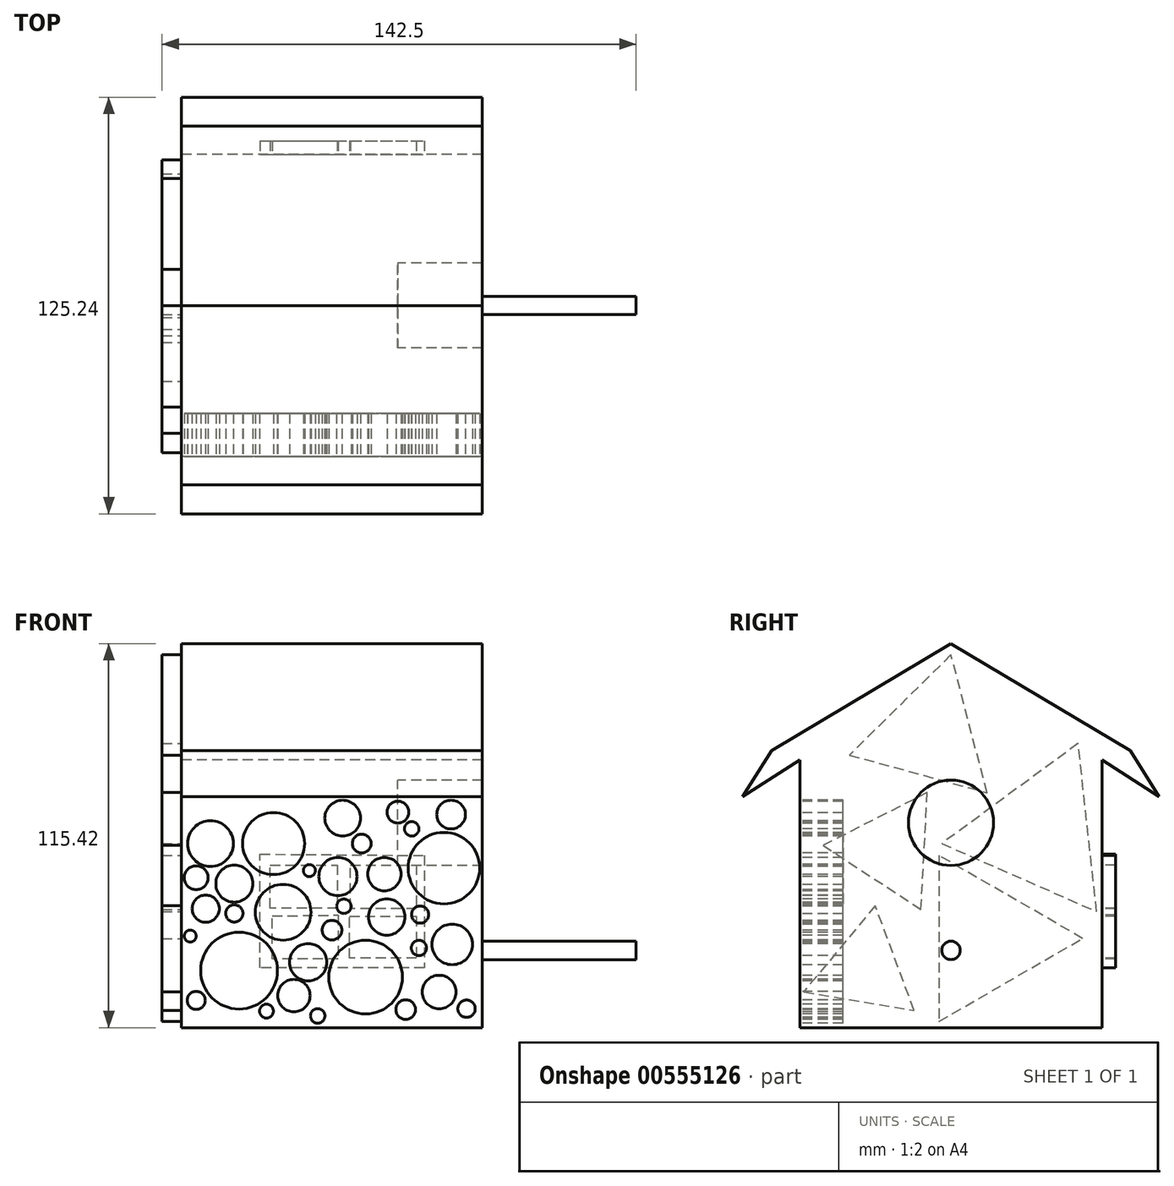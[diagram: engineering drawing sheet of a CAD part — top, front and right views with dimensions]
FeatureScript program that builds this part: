
annotation { "Feature Type Name" : "Feature", "Feature Type Description" : "" }
export const myFeature = defineFeature(function(context is Context, id is Id, definition is map)
    precondition{}
    {
        {
            var Q0;
            Q0=qCreatedBy(makeId("Right.planeOp"),FACE);
            var sketch = newSketch(context, id + "F0", { "sketchPlane" : qUnion([Q0])});
            skLineSegment(sketch, "E0", {"start": v(-45.42, 25.15) * mm, "end": v(0, 50.44) * mm});
            skLineSegment(sketch, "E1.MirrorCS", {"start": v(45.42, 25.15) * mm, "end": v(0, 50.44) * mm});
            skLineSegment(sketch, "E2", {"start": v(-45.42, 25.15) * mm, "end": v(-45.42, -55.32) * mm});
            skLineSegment(sketch, "E3", {"start": v(-45.42, -55.32) * mm, "end": v(45.42, -55.32) * mm});
            skLineSegment(sketch, "E4", {"start": v(45.42, -55.32) * mm, "end": v(45.42, 25.15) * mm});
            skCircle(sketch, "E5", {"center": v(0, 6.25) * mm, "radius": 12.8 * mm});
            skLineSegment(sketch, "E6", {"start": v(-45.42, 25.15) * mm, "end": v(-62.62, 14.07) * mm});
            skLineSegment(sketch, "E7", {"start": v(-62.62, 14.07) * mm, "end": v(-53.87, 27.88) * mm});
            skLineSegment(sketch, "E8", {"start": v(-53.87, 27.88) * mm, "end": v(0, 60.1) * mm});
            skLineSegment(sketch, "E9.MirrorCS", {"start": v(53.87, 27.88) * mm, "end": v(0, 60.1) * mm});
            skLineSegment(sketch, "E10.MirrorCS", {"start": v(62.62, 14.07) * mm, "end": v(53.87, 27.88) * mm});
            skLineSegment(sketch, "E11.MirrorCS", {"start": v(45.42, 25.15) * mm, "end": v(62.62, 14.07) * mm});
            skSolve(sketch);
        }
        {
            var Q0;
            Q0 = qSketchRegion(id + "F0", true);
            extrude(context, id + "F1", {"entities" : qUnion([Q0]), "depth" : 13.46 * mm, "offsetDistance" : 25.4 * mm});
        }
        {
            var Q0;
            Q0=qCreatedBy(makeId("Right.planeOp"),FACE);
            var sketch = newSketch(context, id + "F2", { "sketchPlane" : qUnion([Q0])});
            skCircle(sketch, "E12", {"center": v(0, -32.1) * mm, "radius": 2.78 * mm});
            skSolve(sketch);
        }
        {
            var Q0;
            Q0 = qSketchRegion(id + "F2", true);
            extrude(context, id + "F3", {"entities" : qUnion([Q0]), "operationType" : NewBodyOperationType.ADD, "depth" : 71.63 * mm, "offsetDistance" : 25.4 * mm});
        }
        {
            var Q0;
            Q0 = qSketchRegion(id + "F0", true);
            extrude(context, id + "F4", {"entities" : qUnion([Q0]), "operationType" : NewBodyOperationType.ADD, "depth" : 25.4 * mm, "offsetDistance" : 25.4 * mm});
        }
        {
            var Q0;
            Q0 = qSketchRegion(id + "F0", true);
            extrude(context, id + "F5", {"entities" : qUnion([Q0]), "operationType" : NewBodyOperationType.ADD, "depth" : 25.4 * mm, "offsetDistance" : 25.4 * mm});
        }
        {
            var Q0;
            Q0=makeQuery(id+"F1.opExtrude","CAP_FACE",FACE,{"disambiguationData":[OSD([sQuery(id+"F0.wireOp",EDGE,"E2"),sQuery(id+"F0.wireOp",EDGE,"E3"),sQuery(id+"F0.wireOp",EDGE,"E4"),sQuery(id+"F0.wireOp",EDGE,"E5"),sQuery(id+"F0.wireOp",EDGE,"E6"),sQuery(id+"F0.wireOp",EDGE,"E7"),sQuery(id+"F0.wireOp",EDGE,"E8"),sQuery(id+"F0.wireOp",EDGE,"E9.MirrorCS"),sQuery(id+"F0.wireOp",EDGE,"E10.MirrorCS"),sQuery(id+"F0.wireOp",EDGE,"E11.MirrorCS")])],"isStart":true});
            var sketch = newSketch(context, id + "F6", { "sketchPlane" : qUnion([Q0])});
            skLineSegment(sketch, "E13", {"start": v(0, 60.1) * mm, "end": v(-53.87, 27.88) * mm});
            skLineSegment(sketch, "E14", {"start": v(-53.87, 27.88) * mm, "end": v(-62.62, 14.07) * mm});
            skLineSegment(sketch, "E15", {"start": v(-62.62, 14.07) * mm, "end": v(-45.42, 25.15) * mm});
            skLineSegment(sketch, "E16", {"start": v(-45.42, 25.15) * mm, "end": v(-45.42, -55.32) * mm});
            skLineSegment(sketch, "E17", {"start": v(-45.42, -55.32) * mm, "end": v(45.42, -55.32) * mm});
            skLineSegment(sketch, "E18", {"start": v(45.42, -55.32) * mm, "end": v(45.42, 25.15) * mm});
            skLineSegment(sketch, "E19", {"start": v(45.42, 25.15) * mm, "end": v(62.62, 14.07) * mm});
            skLineSegment(sketch, "E20", {"start": v(62.62, 14.07) * mm, "end": v(53.87, 27.88) * mm});
            skLineSegment(sketch, "E21", {"start": v(53.87, 27.88) * mm, "end": v(0, 60.1) * mm});
            skSolve(sketch);
        }
        {
            var Q0;
            Q0 = qSketchRegion(id + "F6", true);
            extrude(context, id + "F7", {"entities" : qUnion([Q0]), "operationType" : NewBodyOperationType.ADD, "depth" : 65.02 * mm, "offsetDistance" : 25.4 * mm});
        }
        {
            var Q0;
            {var subQ0=sQuery(id+"F0.wireOp",EDGE,"E2");Q0=makeQuery(id+"F7.boolean.opBoolean","MERGE",FACE,{"derivedFrom":[makeQuery(id+"F4.boolean.opBoolean","MERGE",FACE,{"derivedFrom":[makeQuery(id+"F1.opExtrude","SWEPT_FACE",FACE,{"disambiguationData":[OSD([subQ0])]}),makeQuery(id+"F4.opExtrude","SWEPT_FACE",FACE,{"disambiguationData":[OSD([subQ0])]})]}),makeQuery(id+"F7.opExtrude","SWEPT_FACE",FACE,{"disambiguationData":[OSD([sQuery(id+"F6.wireOp",EDGE,"E18")])]})]});}
            var sketch = newSketch(context, id + "F8", { "sketchPlane" : qUnion([Q0])});
            skCircle(sketch, "E22", {"center": v(-47.74, -38.18) * mm, "radius": 11.54 * mm});
            skCircle(sketch, "E23", {"center": v(-49.17, -12.04) * mm, "radius": 5.56 * mm});
            skCircle(sketch, "E24", {"center": v(-34.49, -20.64) * mm, "radius": 8.38 * mm});
            skCircle(sketch, "E25", {"center": v(-37.35, 0) * mm, "radius": 9.32 * mm});
            skCircle(sketch, "E26", {"center": v(13.84, -7.4) * mm, "radius": 10.75 * mm});
            skCircle(sketch, "E27", {"center": v(-16.23, -18.85) * mm, "radius": 2.18 * mm});
            skCircle(sketch, "E28", {"center": v(-26.97, -35.67) * mm, "radius": 5.6 * mm});
            skCircle(sketch, "E29", {"center": v(-3.34, -22.07) * mm, "radius": 5.45 * mm});
            skCircle(sketch, "E30", {"center": v(6.68, -21.35) * mm, "radius": 2.58 * mm});
            skCircle(sketch, "E31", {"center": v(6.32, -31.38) * mm, "radius": 2.3 * mm});
            skCircle(sketch, "E32", {"center": v(16.35, -30.3) * mm, "radius": 6.1 * mm});
            skCircle(sketch, "E33", {"center": v(12.4, -44.62) * mm, "radius": 5.06 * mm});
            skCircle(sketch, "E34", {"center": v(20.64, -49.63) * mm, "radius": 2.6 * mm});
            skCircle(sketch, "E35", {"center": v(-4.06, -9.18) * mm, "radius": 5.02 * mm});
            skCircle(sketch, "E36", {"center": v(-26.61, -8.1) * mm, "radius": 1.83 * mm});
            skCircle(sketch, "E37", {"center": v(-18.02, -9.9) * mm, "radius": 5.74 * mm});
            skCircle(sketch, "E38", {"center": v(-16.6, 7.64) * mm, "radius": 5.38 * mm});
            skCircle(sketch, "E39", {"center": v(0, 9.43) * mm, "radius": 3.28 * mm});
            skCircle(sketch, "E40", {"center": v(15.99, 8.72) * mm, "radius": 4.31 * mm});
            skCircle(sketch, "E41", {"center": v(4.17, 4.42) * mm, "radius": 2.18 * mm});
            skCircle(sketch, "E42", {"center": v(-10.86, 0) * mm, "radius": 2.83 * mm});
            skCircle(sketch, "E43", {"center": v(-56.33, 0) * mm, "radius": 6.87 * mm});
            skCircle(sketch, "E44", {"center": v(-60.62, -10.25) * mm, "radius": 3.58 * mm});
            skCircle(sketch, "E45", {"center": v(-49.17, -21) * mm, "radius": 2.58 * mm});
            skCircle(sketch, "E46", {"center": v(-57.76, -19.56) * mm, "radius": 4.08 * mm});
            skCircle(sketch, "E47", {"center": v(-31.27, -45.7) * mm, "radius": 4.87 * mm});
            skCircle(sketch, "E48", {"center": v(-19.81, -26) * mm, "radius": 2.95 * mm});
            skCircle(sketch, "E49", {"center": v(-24.1, -51.78) * mm, "radius": 2.18 * mm});
            skCircle(sketch, "E50", {"center": v(-60.62, -47.13) * mm, "radius": 2.73 * mm});
            skCircle(sketch, "E51", {"center": v(-62.41, -27.8) * mm, "radius": 1.79 * mm});
            skCircle(sketch, "E52", {"center": v(-39.5, -50.35) * mm, "radius": 2.09 * mm});
            skCircle(sketch, "E53", {"center": v(-9.7, -40.14) * mm, "radius": 11.07 * mm});
            skCircle(sketch, "E54", {"center": v(2.34, -49.89) * mm, "radius": 2.95 * mm});
            skSolve(sketch);
        }
        {
            var Q0;
            Q0 = qSketchRegion(id + "F8", true);
            extrude(context, id + "F9", {"entities" : qUnion([Q0]), "operationType" : NewBodyOperationType.REMOVE, "oppositeDirection" : true, "depth" : 12.95 * mm, "offsetDistance" : 25.4 * mm});
        }
        {
            var Q0;
            {var subQ0=sQuery(id+"F0.wireOp",EDGE,"E4");Q0=makeQuery(id+"F7.boolean.opBoolean","MERGE",FACE,{"derivedFrom":[makeQuery(id+"F4.boolean.opBoolean","MERGE",FACE,{"derivedFrom":[makeQuery(id+"F1.opExtrude","SWEPT_FACE",FACE,{"disambiguationData":[OSD([subQ0])]}),makeQuery(id+"F4.opExtrude","SWEPT_FACE",FACE,{"disambiguationData":[OSD([subQ0])]})]}),makeQuery(id+"F7.opExtrude","SWEPT_FACE",FACE,{"disambiguationData":[OSD([sQuery(id+"F6.wireOp",EDGE,"E16")])]})]});}
            var sketch = newSketch(context, id + "F10", { "sketchPlane" : qUnion([Q0])});
            skLineSegment(sketch, "E55", {"start": v(-7.92, -3.58) * mm, "end": v(-7.92, -37.33) * mm});
            skLineSegment(sketch, "E56", {"start": v(-7.92, -37.33) * mm, "end": v(41.41, -37.33) * mm});
            skLineSegment(sketch, "E57", {"start": v(41.41, -37.33) * mm, "end": v(41.41, -3.2) * mm});
            skLineSegment(sketch, "E58", {"start": v(41.41, -3.2) * mm, "end": v(-7.92, -3.58) * mm});
            skLineSegment(sketch, "E59", {"start": v(-5.57, -6.46) * mm, "end": v(-5.57, -19.52) * mm});
            skLineSegment(sketch, "E60", {"start": v(-5.57, -19.52) * mm, "end": v(14.23, -19.52) * mm});
            skLineSegment(sketch, "E61", {"start": v(14.23, -19.52) * mm, "end": v(14.23, -6.46) * mm});
            skLineSegment(sketch, "E62", {"start": v(14.23, -6.46) * mm, "end": v(-5.57, -6.46) * mm});
            skLineSegment(sketch, "E63", {"start": v(18.2, -6.46) * mm, "end": v(18.2, -19.4) * mm});
            skLineSegment(sketch, "E64", {"start": v(18.2, -19.4) * mm, "end": v(38.4, -19.4) * mm});
            skLineSegment(sketch, "E65", {"start": v(38.4, -19.4) * mm, "end": v(38.4, -6.46) * mm});
            skLineSegment(sketch, "E66", {"start": v(38.4, -6.46) * mm, "end": v(18.2, -6.46) * mm});
            skLineSegment(sketch, "E67", {"start": v(-5.57, -22.56) * mm, "end": v(-5.57, -34.44) * mm});
            skLineSegment(sketch, "E68", {"start": v(-5.57, -34.44) * mm, "end": v(13.57, -34.44) * mm});
            skLineSegment(sketch, "E69", {"start": v(13.57, -34.44) * mm, "end": v(14.5, -34.44) * mm});
            skLineSegment(sketch, "E70", {"start": v(14.5, -34.44) * mm, "end": v(14.5, -23.22) * mm});
            skLineSegment(sketch, "E71", {"start": v(14.5, -23.22) * mm, "end": v(14.5, -21.9) * mm});
            skLineSegment(sketch, "E72", {"start": v(14.5, -21.9) * mm, "end": v(-5.57, -21.9) * mm});
            skLineSegment(sketch, "E73", {"start": v(17.93, -21.5) * mm, "end": v(17.93, -34.7) * mm});
            skLineSegment(sketch, "E74", {"start": v(17.93, -34.7) * mm, "end": v(37.73, -34.7) * mm});
            skLineSegment(sketch, "E75", {"start": v(37.73, -34.7) * mm, "end": v(37.73, -21.77) * mm});
            skLineSegment(sketch, "E76", {"start": v(37.73, -21.77) * mm, "end": v(17.93, -21.5) * mm});
            skLineSegment(sketch, "E77", {"start": v(-5.57, -21.9) * mm, "end": v(-5.57, -22.56) * mm});
            skSolve(sketch);
        }
        {
            var Q0;
            Q0 = qSketchRegion(id + "F10", true);
            extrude(context, id + "F11", {"entities" : qUnion([Q0]), "operationType" : NewBodyOperationType.ADD, "depth" : 4.06 * mm, "offsetDistance" : 25.4 * mm});
        }
        {
            var Q0;
            Q0=makeQuery(id+"F7.opExtrude","CAP_FACE",FACE,{"disambiguationData":[OSD([sQuery(id+"F6.wireOp",EDGE,"E13"),sQuery(id+"F6.wireOp",EDGE,"E14"),sQuery(id+"F6.wireOp",EDGE,"E15"),sQuery(id+"F6.wireOp",EDGE,"E16"),sQuery(id+"F6.wireOp",EDGE,"E17"),sQuery(id+"F6.wireOp",EDGE,"E18"),sQuery(id+"F6.wireOp",EDGE,"E19"),sQuery(id+"F6.wireOp",EDGE,"E20"),sQuery(id+"F6.wireOp",EDGE,"E21")])],"isStart":false});
            var sketch = newSketch(context, id + "F12", { "sketchPlane" : qUnion([Q0])});
            skCircle(sketch, "E78.cCircle", {"center": v(-26.42, 3.21) * mm, "radius": 14.67 * mm, "construction": true});
            skLineSegment(sketch, "E78.0", {"start": v(2.75, 0) * mm, "end": v(-43.79, -20.44) * mm});
            skLineSegment(sketch, "E78.1", {"start": v(-43.79, -20.44) * mm, "end": v(-38.22, 30.08) * mm});
            skLineSegment(sketch, "E78.2", {"start": v(-38.22, 30.08) * mm, "end": v(2.75, 0) * mm});
            skPoint(sketch, "E78.0.midPoint", {"position": v(-20.52, -10.22) * mm});
            skCircle(sketch, "E79.cCircle", {"center": v(-10.8, -28.51) * mm, "radius": 14.4 * mm, "construction": true});
            skLineSegment(sketch, "E79.0", {"start": v(3.6, -3.57) * mm, "end": v(3.6, -53.45) * mm});
            skLineSegment(sketch, "E79.1", {"start": v(3.6, -53.45) * mm, "end": v(-39.6, -28.51) * mm});
            skLineSegment(sketch, "E79.2", {"start": v(-39.6, -28.51) * mm, "end": v(3.6, -3.57) * mm});
            skPoint(sketch, "E79.0.midPoint", {"position": v(3.6, -28.51) * mm});
            skCircle(sketch, "E80.cCircle", {"center": v(26.02, -37.78) * mm, "radius": 9.7 * mm, "construction": true});
            skLineSegment(sketch, "E80.0", {"start": v(11.06, -50.16) * mm, "end": v(22.78, -18.64) * mm});
            skLineSegment(sketch, "E80.1", {"start": v(22.78, -18.64) * mm, "end": v(44.22, -44.54) * mm});
            skLineSegment(sketch, "E80.2", {"start": v(44.22, -44.54) * mm, "end": v(11.06, -50.16) * mm});
            skPoint(sketch, "E80.0.midPoint", {"position": v(16.92, -34.4) * mm});
            skCircle(sketch, "E81.cCircle", {"center": v(18.2, -1.67) * mm, "radius": 10.15 * mm, "construction": true});
            skLineSegment(sketch, "E81.0", {"start": v(38.46, -0.56) * mm, "end": v(9.03, -19.77) * mm});
            skLineSegment(sketch, "E81.1", {"start": v(9.03, -19.77) * mm, "end": v(7.11, 15.33) * mm});
            skLineSegment(sketch, "E81.2", {"start": v(7.11, 15.33) * mm, "end": v(38.46, -0.56) * mm});
            skPoint(sketch, "E81.0.midPoint", {"position": v(23.75, -10.16) * mm});
            skCircle(sketch, "E82.cCircle", {"center": v(6.54, 32.87) * mm, "radius": 12.38 * mm, "construction": true});
            skLineSegment(sketch, "E82.0", {"start": v(-10.86, 15.27) * mm, "end": v(0, 56.75) * mm});
            skLineSegment(sketch, "E82.1", {"start": v(0, 56.75) * mm, "end": v(30.5, 26.6) * mm});
            skLineSegment(sketch, "E82.2", {"start": v(30.5, 26.6) * mm, "end": v(-10.86, 15.27) * mm});
            skPoint(sketch, "E82.0.midPoint", {"position": v(-5.43, 36) * mm});
            skSolve(sketch);
        }
        {
            var Q0;
            Q0 = qSketchRegion(id + "F12", true);
            extrude(context, id + "F13", {"entities" : qUnion([Q0]), "operationType" : NewBodyOperationType.ADD, "depth" : 5.84 * mm, "offsetDistance" : 25.4 * mm});
        }
    });
